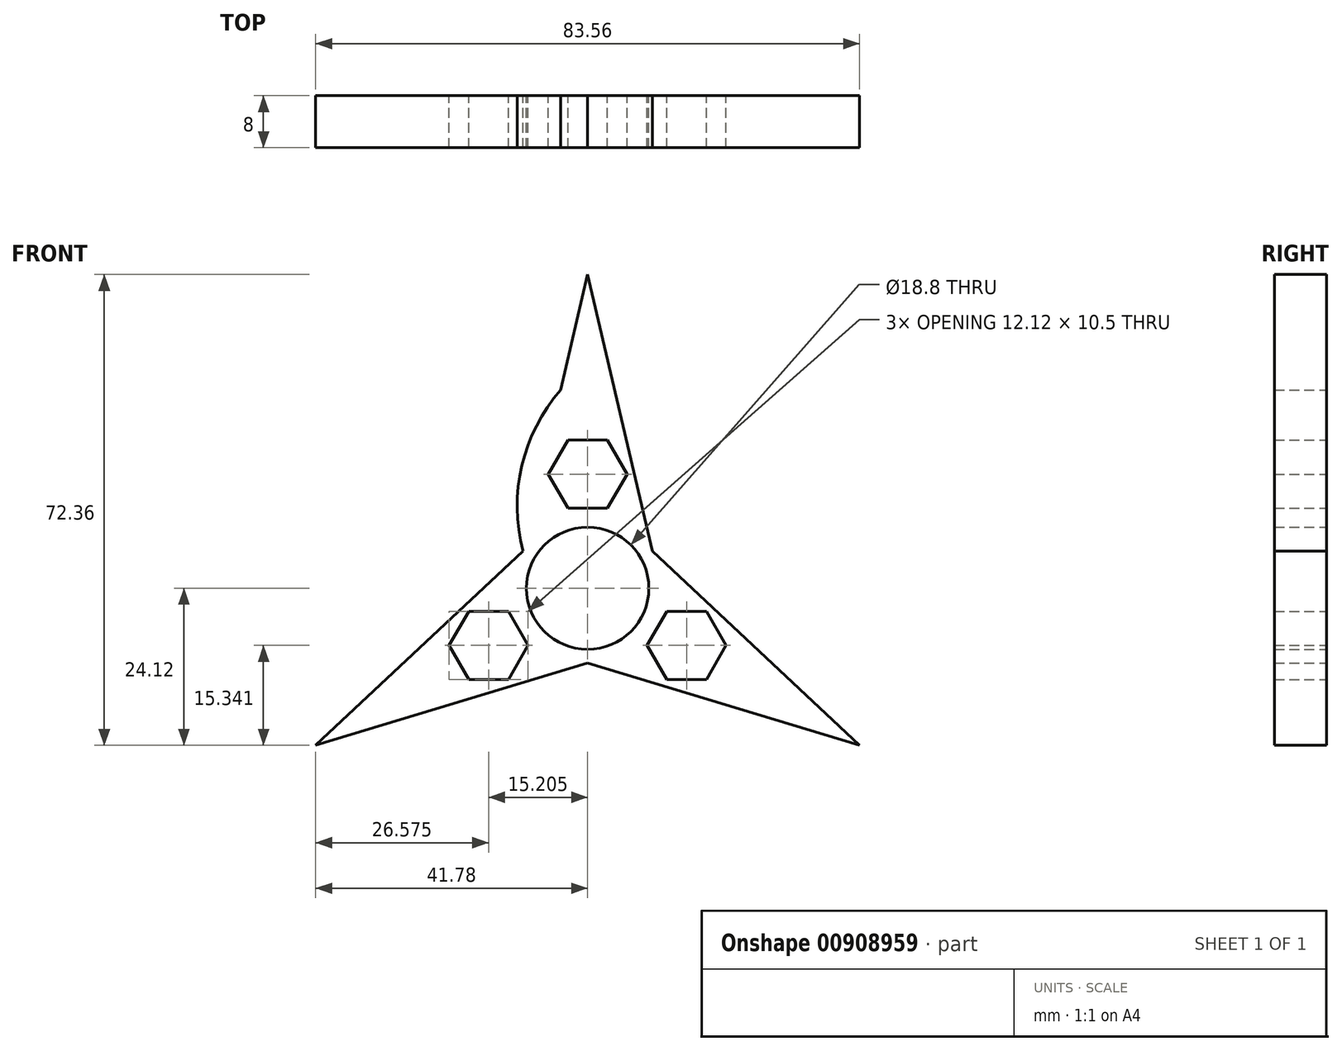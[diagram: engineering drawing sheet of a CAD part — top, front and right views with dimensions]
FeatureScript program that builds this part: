
annotation { "Feature Type Name" : "Feature", "Feature Type Description" : "" }
export const myFeature = defineFeature(function(context is Context, id is Id, definition is map)
    precondition{}
    {
        {
            var Q0;
            Q0=qCreatedBy(makeId("Front.planeOp"),FACE);
            var sketch = newSketch(context, id + "F0", { "sketchPlane" : qUnion([Q0])});
            skCircle(sketch, "E0", {"center": v(0, 0) * mm, "radius": 9.4 * mm});
            skCircle(sketch, "E1.cCircle", {"center": v(0, 17.56) * mm, "radius": 5.25 * mm, "construction": true});
            skLineSegment(sketch, "E1.0", {"start": v(3.03, 12.3) * mm, "end": v(-3.03, 12.3) * mm});
            skLineSegment(sketch, "E1.1", {"start": v(-3.03, 12.3) * mm, "end": v(-6.06, 17.56) * mm});
            skLineSegment(sketch, "E1.2", {"start": v(-6.06, 17.56) * mm, "end": v(-3.03, 22.8) * mm});
            skLineSegment(sketch, "E1.3", {"start": v(-3.03, 22.8) * mm, "end": v(3.03, 22.8) * mm});
            skLineSegment(sketch, "E1.4", {"start": v(3.03, 22.8) * mm, "end": v(6.06, 17.56) * mm});
            skLineSegment(sketch, "E1.5", {"start": v(6.06, 17.56) * mm, "end": v(3.03, 12.3) * mm});
            skPoint(sketch, "E1.0.midPoint", {"position": v(0, 12.3) * mm});
            skLineSegment(sketch, "E2.1.2", {"start": v(-18.24, -14.03) * mm, "end": v(-21.27, -8.78) * mm});
            skLineSegment(sketch, "E2.1.3", {"start": v(-21.27, -8.78) * mm, "end": v(-18.24, -3.53) * mm});
            skCircle(sketch, "E2.1.4", {"center": v(-15.2, -8.78) * mm, "radius": 5.25 * mm, "construction": true});
            skLineSegment(sketch, "E2.1.5", {"start": v(-18.24, -3.53) * mm, "end": v(-12.17, -3.53) * mm});
            skLineSegment(sketch, "E2.1.6", {"start": v(-12.17, -3.53) * mm, "end": v(-9.14, -8.78) * mm});
            skLineSegment(sketch, "E2.1.7", {"start": v(-9.14, -8.78) * mm, "end": v(-12.17, -14.03) * mm});
            skLineSegment(sketch, "E2.1.8", {"start": v(-12.17, -14.03) * mm, "end": v(-18.24, -14.03) * mm});
            skLineSegment(sketch, "E2.2.2", {"start": v(21.27, -8.78) * mm, "end": v(18.24, -14.03) * mm});
            skLineSegment(sketch, "E2.2.3", {"start": v(18.24, -14.03) * mm, "end": v(12.17, -14.03) * mm});
            skCircle(sketch, "E2.2.4", {"center": v(15.2, -8.78) * mm, "radius": 5.25 * mm, "construction": true});
            skLineSegment(sketch, "E2.2.5", {"start": v(12.17, -14.03) * mm, "end": v(9.14, -8.78) * mm});
            skLineSegment(sketch, "E2.2.6", {"start": v(9.14, -8.78) * mm, "end": v(12.17, -3.53) * mm});
            skLineSegment(sketch, "E2.2.7", {"start": v(12.17, -3.53) * mm, "end": v(18.24, -3.53) * mm});
            skLineSegment(sketch, "E2.2.8", {"start": v(18.24, -3.53) * mm, "end": v(21.27, -8.78) * mm});
            skLineSegment(sketch, "E3", {"start": v(-9.94, 5.74) * mm, "end": v(0, 48.24) * mm});
            skLineSegment(sketch, "E4.MirrorCS", {"start": v(9.94, 5.74) * mm, "end": v(0, 48.24) * mm});
            skLineSegment(sketch, "E5.1.0", {"start": v(0, -11.48) * mm, "end": v(-41.78, -24.12) * mm});
            skLineSegment(sketch, "E5.1.1", {"start": v(-9.94, 5.74) * mm, "end": v(-41.78, -24.12) * mm});
            skLineSegment(sketch, "E5.2.0", {"start": v(9.94, 5.74) * mm, "end": v(41.78, -24.12) * mm});
            skLineSegment(sketch, "E5.2.1", {"start": v(0, -11.48) * mm, "end": v(41.78, -24.12) * mm});
            skArc(sketch, "E6", {"start": v(-4.15, 30.5) * mm, "mid": v(-10.1, 18.83) * mm, "end": v(-9.94, 5.74) * mm});
            skSolve(sketch);
        }
        {
            var Q0;
            {var subQ1=sQuery(id+"F0.wireOp",EDGE,"E2.1.0");Q0=makeQuery(id+"F0.imprint","IMPRINT",FACE,{"disambiguationData":[TD([[makeQuery(id+"F0.imprint","IMPRINT",EDGE,{"derivedFrom":subQ1}),-1.0]])]});}
            var Q1;
            {var subQ1=sQuery(id+"F0.wireOp",EDGE,"E2.2.0");Q1=makeQuery(id+"F0.imprint","IMPRINT",FACE,{"disambiguationData":[TD([[makeQuery(id+"F0.imprint","IMPRINT",EDGE,{"derivedFrom":subQ1}),-1.0]])]});}
            var Q2;
            Q2=makeQuery(id+"F0.imprint","IMPRINT",FACE,{"disambiguationData":[TD([[makeQuery(id+"F0.imprint","IMPRINT",EDGE,{"derivedFrom":sQuery(id+"F0.wireOp",EDGE,"E0")}),-1.0]])]});
            var Q3;
            {var subQ1=sQuery(id+"F0.wireOp",EDGE,"KgVObCfJ-5joL-1ZzJ-WEhS-nYP76a5kcPh3");Q3=makeQuery(id+"F0.imprint","IMPRINT",FACE,{"disambiguationData":[TD([[makeQuery(id+"F0.imprint","IMPRINT",EDGE,{"derivedFrom":subQ1}),-1.0]])]});}
            extrude(context, id + "F1", {"entities" : qUnion([Q0, Q1, Q2, Q3]), "depth" : 8 * mm, "offsetDistance" : 25 * mm});
        }
        {
            var Q0;
            Q0 = qSketchRegion(id + "F0", true);
            extrude(context, id + "F2", {"entities" : qUnion([Q0]), "operationType" : NewBodyOperationType.ADD, "depth" : 8 * mm, "offsetDistance" : 25 * mm});
        }
    });
